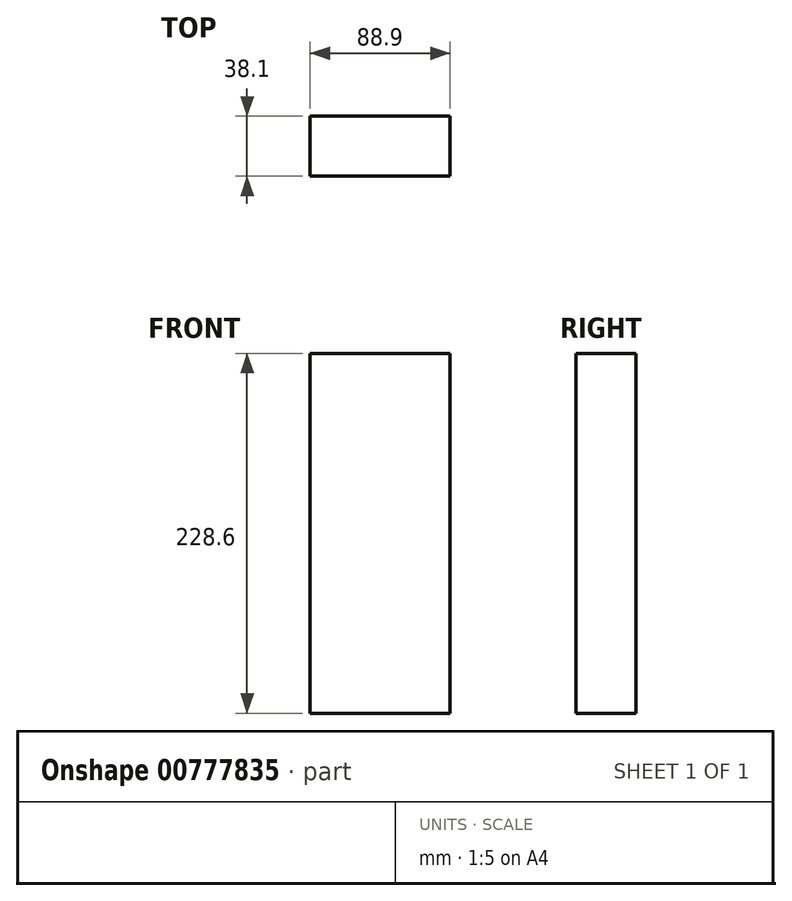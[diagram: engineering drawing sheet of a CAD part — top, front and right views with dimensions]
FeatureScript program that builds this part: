
annotation { "Feature Type Name" : "Feature", "Feature Type Description" : "" }
export const myFeature = defineFeature(function(context is Context, id is Id, definition is map)
    precondition{}
    {
        {
            var Q0;
            Q0=qCreatedBy(makeId("Top.planeOp"),FACE);
            var sketch = newSketch(context, id + "F0", { "sketchPlane" : qUnion([Q0])});
            skLineSegment(sketch, "E0.bottom", {"start": v(-44.45, -19.05) * mm, "end": v(44.45, -19.05) * mm});
            skLineSegment(sketch, "E0.top", {"start": v(-44.45, 19.05) * mm, "end": v(44.45, 19.05) * mm});
            skLineSegment(sketch, "E0.left", {"start": v(-44.45, -19.05) * mm, "end": v(-44.45, 19.05) * mm});
            skLineSegment(sketch, "E0.right", {"start": v(44.45, -19.05) * mm, "end": v(44.45, 19.05) * mm});
            skPoint(sketch, "E0.middle", {"position": v(0, 0) * mm});
            skSolve(sketch);
        }
        {
            var Q0;
            Q0 = qSketchRegion(id + "F0", true);
            extrude(context, id + "F1", {"entities" : qUnion([Q0]), "endBound" : BoundingType.SYMMETRIC, "depth" : 228.6 * mm, "offsetDistance" : 25.4 * mm});
        }
    });
